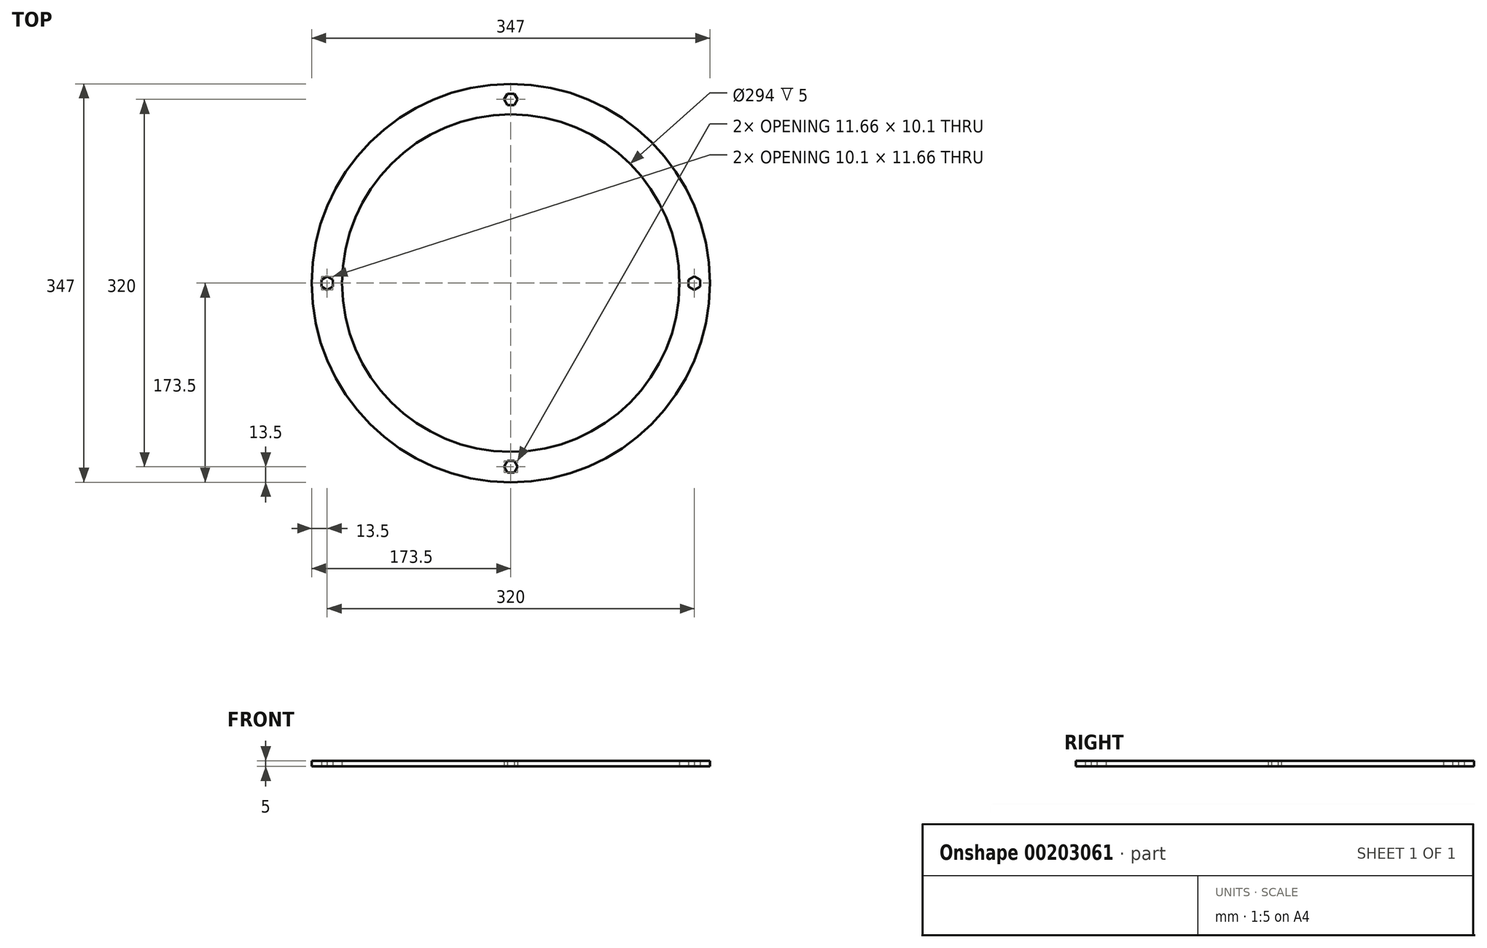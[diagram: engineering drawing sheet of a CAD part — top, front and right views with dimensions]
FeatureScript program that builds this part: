
annotation { "Feature Type Name" : "Feature", "Feature Type Description" : "" }
export const myFeature = defineFeature(function(context is Context, id is Id, definition is map)
    precondition{}
    {
        {
            var Q0;
            Q0=qCreatedBy(makeId("Top.planeOp"),FACE);
            var sketch = newSketch(context, id + "F0", { "sketchPlane" : qUnion([Q0])});
            skCircle(sketch, "E0", {"center": v(0, 0) * mm, "radius": 173.5 * mm});
            skCircle(sketch, "E1", {"center": v(0, 0) * mm, "radius": 147 * mm});
            skCircle(sketch, "E2.cCircle", {"center": v(-160, 0) * mm, "radius": 5.05 * mm, "construction": true});
            skLineSegment(sketch, "E2.0", {"start": v(-154.95, 2.92) * mm, "end": v(-154.95, -2.92) * mm});
            skLineSegment(sketch, "E2.1", {"start": v(-154.95, -2.92) * mm, "end": v(-160, -5.83) * mm});
            skLineSegment(sketch, "E2.2", {"start": v(-160, -5.83) * mm, "end": v(-165.05, -2.92) * mm});
            skLineSegment(sketch, "E2.3", {"start": v(-165.05, -2.92) * mm, "end": v(-165.05, 2.92) * mm});
            skLineSegment(sketch, "E2.4", {"start": v(-165.05, 2.92) * mm, "end": v(-160, 5.83) * mm});
            skLineSegment(sketch, "E2.5", {"start": v(-160, 5.83) * mm, "end": v(-154.95, 2.92) * mm});
            skPoint(sketch, "E2.0.midPoint", {"position": v(-154.95, 0) * mm});
            skCircle(sketch, "E3.cCircle", {"center": v(160, 0) * mm, "radius": 5.05 * mm, "construction": true});
            skLineSegment(sketch, "E3.0", {"start": v(154.95, -2.92) * mm, "end": v(154.95, 2.92) * mm});
            skLineSegment(sketch, "E3.1", {"start": v(154.95, 2.92) * mm, "end": v(160, 5.83) * mm});
            skLineSegment(sketch, "E3.2", {"start": v(160, 5.83) * mm, "end": v(165.05, 2.92) * mm});
            skLineSegment(sketch, "E3.3", {"start": v(165.05, 2.92) * mm, "end": v(165.05, -2.92) * mm});
            skLineSegment(sketch, "E3.4", {"start": v(165.05, -2.92) * mm, "end": v(160, -5.83) * mm});
            skLineSegment(sketch, "E3.5", {"start": v(160, -5.83) * mm, "end": v(154.95, -2.92) * mm});
            skPoint(sketch, "E3.0.midPoint", {"position": v(154.95, 0) * mm});
            skCircle(sketch, "E4.cCircle", {"center": v(0, -160) * mm, "radius": 5.05 * mm, "construction": true});
            skLineSegment(sketch, "E4.0", {"start": v(-2.92, -154.95) * mm, "end": v(2.92, -154.95) * mm});
            skLineSegment(sketch, "E4.1", {"start": v(2.92, -154.95) * mm, "end": v(5.83, -160) * mm});
            skLineSegment(sketch, "E4.2", {"start": v(5.83, -160) * mm, "end": v(2.92, -165.05) * mm});
            skLineSegment(sketch, "E4.3", {"start": v(2.92, -165.05) * mm, "end": v(-2.92, -165.05) * mm});
            skLineSegment(sketch, "E4.4", {"start": v(-2.92, -165.05) * mm, "end": v(-5.83, -160) * mm});
            skLineSegment(sketch, "E4.5", {"start": v(-5.83, -160) * mm, "end": v(-2.92, -154.95) * mm});
            skPoint(sketch, "E4.0.midPoint", {"position": v(0, -154.95) * mm});
            skCircle(sketch, "E5.cCircle", {"center": v(0, 160) * mm, "radius": 5.05 * mm, "construction": true});
            skLineSegment(sketch, "E5.0", {"start": v(2.92, 154.95) * mm, "end": v(-2.92, 154.95) * mm});
            skLineSegment(sketch, "E5.1", {"start": v(-2.92, 154.95) * mm, "end": v(-5.83, 160) * mm});
            skLineSegment(sketch, "E5.2", {"start": v(-5.83, 160) * mm, "end": v(-2.92, 165.05) * mm});
            skLineSegment(sketch, "E5.3", {"start": v(-2.92, 165.05) * mm, "end": v(2.92, 165.05) * mm});
            skLineSegment(sketch, "E5.4", {"start": v(2.92, 165.05) * mm, "end": v(5.83, 160) * mm});
            skLineSegment(sketch, "E5.5", {"start": v(5.83, 160) * mm, "end": v(2.92, 154.95) * mm});
            skPoint(sketch, "E5.0.midPoint", {"position": v(0, 154.95) * mm});
            skSolve(sketch);
        }
        {
            var Q0;
            Q0=makeQuery(id+"F0.imprint","IMPRINT",FACE,{"disambiguationData":[TD([[makeQuery(id+"F0.imprint","IMPRINT",EDGE,{"derivedFrom":sQuery(id+"F0.wireOp",EDGE,"E0")}),1.0]])]});
            extrude(context, id + "F1", {"entities" : qUnion([Q0]), "depth" : 5 * mm});
        }
    });
